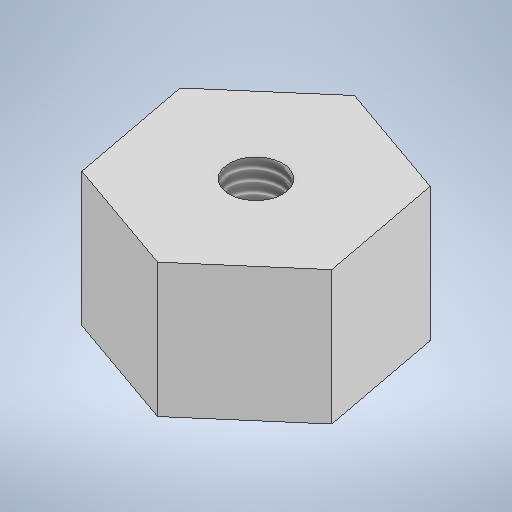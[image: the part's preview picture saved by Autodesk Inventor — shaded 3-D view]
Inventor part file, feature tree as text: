
AUTODESK INVENTOR PART (.ipt)
format: ipt  version: 2025.2 (Build 292293000, 293)  size: 208,896 bytes
history: native  units: mm
features: extrude x2, sketch x2, other x1, thread x1
ambient origin geometry x8: Origin, YZ Plane, XZ Plane, XY Plane, X Axis, Y Axis, Z Axis, Center Point
bodies: Body1 (feature_tree)
feature tree (6):
  other  "Bryła1"
  extrude  "Wyciągnięcie proste1"  Depth=4.0mm
  extrude  "Wyciągnięcie proste2"  Depth=3.5mm
  thread  "Gwint1"
  sketch  "Szkic1"
  sketch  "Szkic2"
